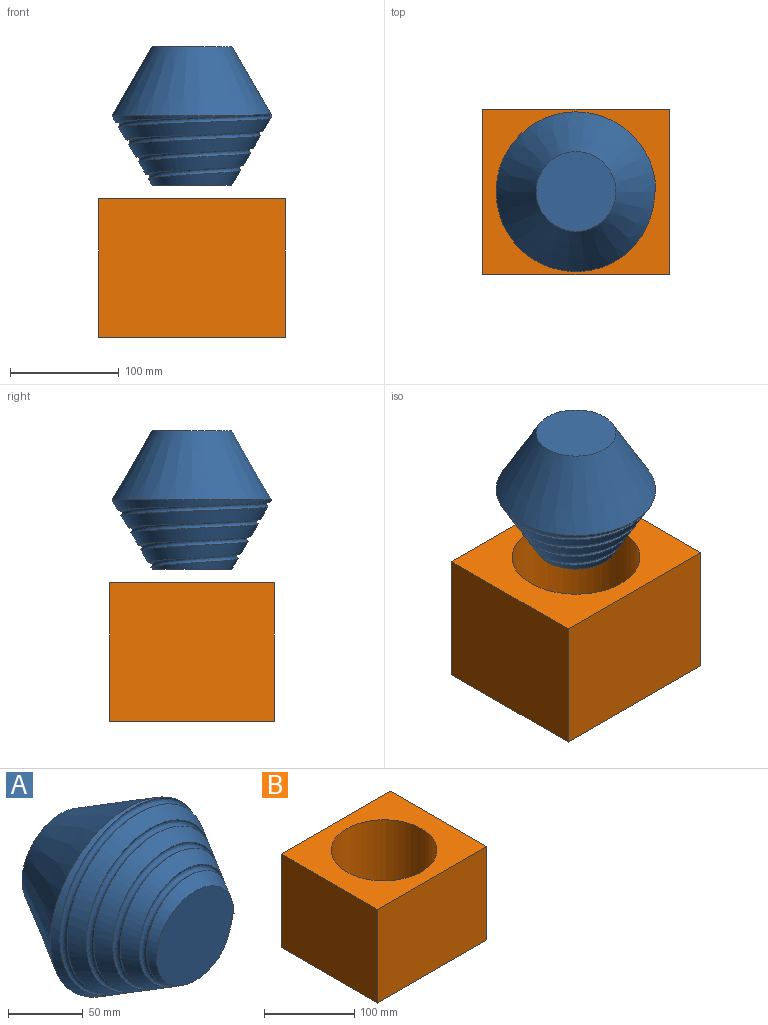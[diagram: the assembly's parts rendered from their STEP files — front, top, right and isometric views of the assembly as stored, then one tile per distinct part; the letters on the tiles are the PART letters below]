
ASSEMBLY  parts=2 mates=1
PART A: 7 faces, bbox 149.2x132.2x147.3 mm
  f0: cone r=36.66mm half-angle=30deg, axis (0,-1,0), area 25235.3mm2, adj f1,f2,f5,f6
  f1: cone r=73.32mm half-angle=30deg, axis (0,1,0), area 18366.5mm2, adj f0,f3,f4,f5,f6
  f2: plane 73.32x73.32mm, normal (0,1,0), area 4222.6mm2, adj f0
  f3: plane 73.32x73.32mm, normal (0,-1,0), area 4173.4mm2, adj f1,f4,f6
  f4: plane 3.86x2.58mm, normal (0,0,-1), area 6.9mm2, adj f1,f3,f6
  f5: plane 4.46x2.58mm, normal (0.02,0,1), area 6.9mm2, adj f0,f1,f6
  f6: bspline ~147.63x143.42mm, area 10760.6mm2, adj f0,f1,f3,f4,f5
PART B: 7 faces, bbox 171.4x151.2x127 mm
  f0: plane 151.2x127mm, normal (1,0,0), area 19202.4mm2, adj f1,f3,f4,f5
  f1: plane 171.42x127mm, normal (0,1,0), area 21770.4mm2, adj f0,f2,f4,f5
  f2: plane 151.2x127mm, normal (-1,0,0), area 19202.4mm2, adj f1,f3,f4,f5
  f3: plane 171.42x127mm, normal (0,-1,0), area 21770.4mm2, adj f0,f2,f4,f5
  f4: plane 171.42x151.2mm, normal (0,0,1), area 15089.5mm2, adj f0,f1,f2,f3,f6
  f5: plane 171.42x151.2mm, normal (0,0,-1), area 15089.5mm2, adj f0,f1,f2,f3,f6
  f6: cylinder r=58.71mm len=127mm, axis (0,0,1), area 46849.9mm2, adj f4,f5
PLACE A rot(axis=(1,0,0),90deg) t=(102.89,-2.7,287.09)mm
PLACE B t=(102.89,-2.7,84.02)mm
MATE cylindrical B.f6 <-> A.f0  axis (0,0,1) through (102.89,-2.7,211.02)mm
